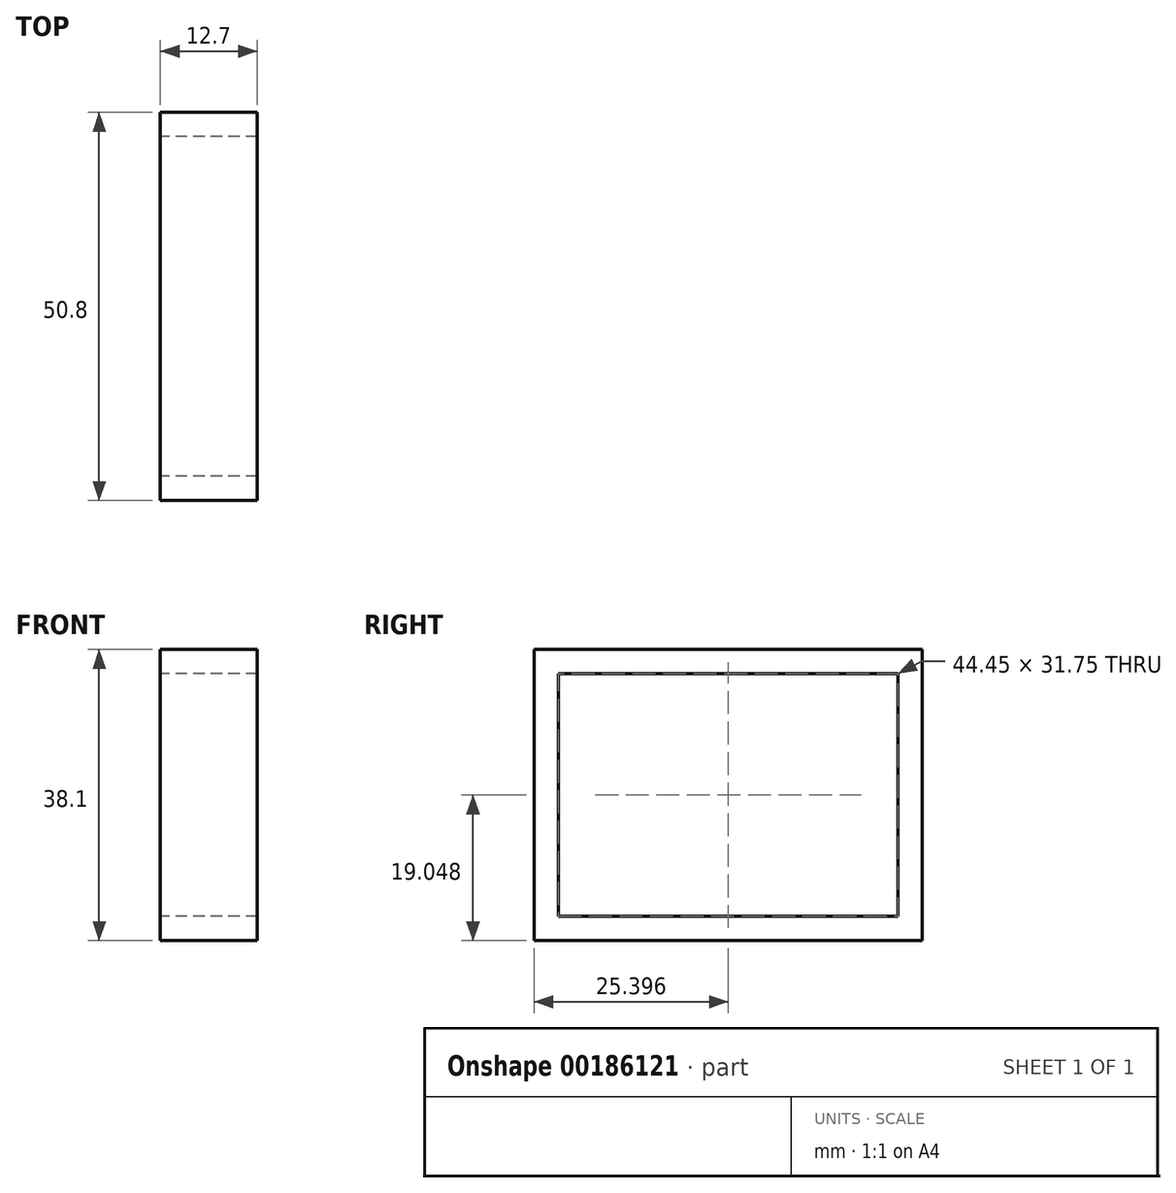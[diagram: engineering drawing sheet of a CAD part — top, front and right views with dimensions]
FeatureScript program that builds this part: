
annotation { "Feature Type Name" : "Feature", "Feature Type Description" : "" }
export const myFeature = defineFeature(function(context is Context, id is Id, definition is map)
    precondition{}
    {
        {
            var Q0;
            Q0=qCreatedBy(makeId("Right.planeOp"),FACE);
            var sketch = newSketch(context, id + "F0", { "sketchPlane" : qUnion([Q0])});
            skLineSegment(sketch, "E0.bottom", {"start": v(-20.23, 18.68) * mm, "end": v(30.57, 18.68) * mm});
            skLineSegment(sketch, "E0.top", {"start": v(-20.23, -19.42) * mm, "end": v(30.57, -19.42) * mm});
            skLineSegment(sketch, "E0.left", {"start": v(-20.23, 18.68) * mm, "end": v(-20.23, -19.42) * mm});
            skLineSegment(sketch, "E0.right", {"start": v(30.57, 18.68) * mm, "end": v(30.57, -19.42) * mm});
            skLineSegment(sketch, "E1.bottom", {"start": v(-17.06, 15.5) * mm, "end": v(27.4, 15.5) * mm});
            skLineSegment(sketch, "E1.top", {"start": v(-17.06, -16.25) * mm, "end": v(27.4, -16.25) * mm});
            skLineSegment(sketch, "E1.left", {"start": v(-17.06, 15.5) * mm, "end": v(-17.06, -16.25) * mm});
            skLineSegment(sketch, "E1.right", {"start": v(27.4, 15.5) * mm, "end": v(27.4, -16.25) * mm});
            skSolve(sketch);
        }
        {
            var Q0;
            Q0=makeQuery(id+"F0.imprint","IMPRINT",FACE,{"disambiguationData":[TD([[makeQuery(id+"F0.imprint","IMPRINT",EDGE,{"derivedFrom":sQuery(id+"F0.wireOp",EDGE,"E0.bottom")}),-1.0]])]});
            extrude(context, id + "F1", {"entities" : qUnion([Q0]), "depth" : 12.7 * mm});
        }
    });
